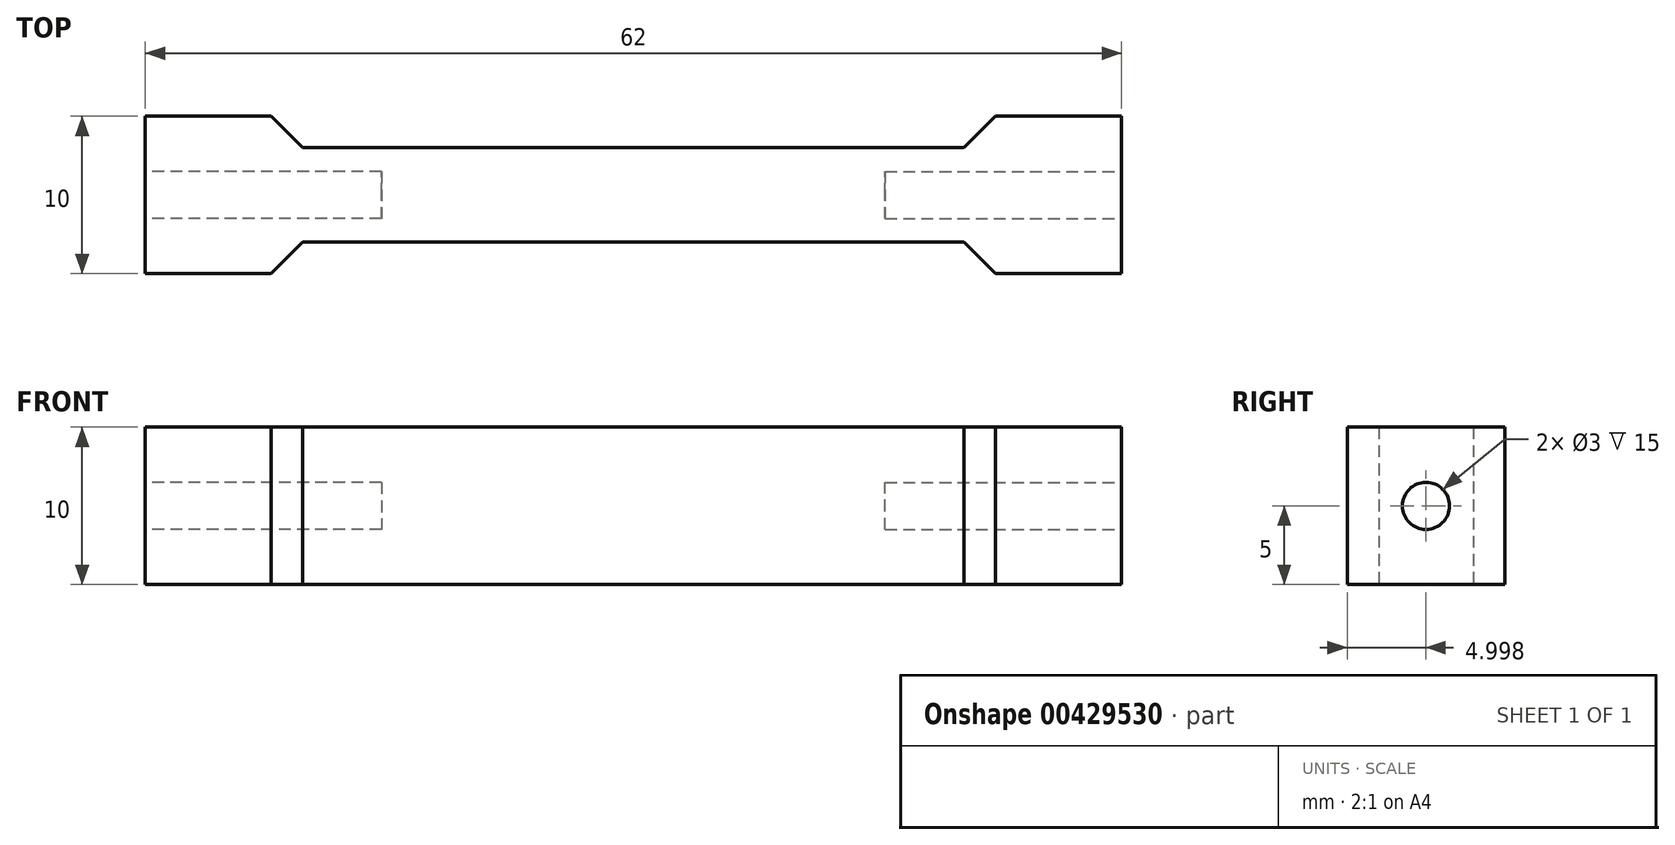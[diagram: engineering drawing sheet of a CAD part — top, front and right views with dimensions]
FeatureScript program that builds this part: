
annotation { "Feature Type Name" : "Feature", "Feature Type Description" : "" }
export const myFeature = defineFeature(function(context is Context, id is Id, definition is map)
    precondition{}
    {
        {
            var Q0;
            Q0=qCreatedBy(makeId("Top.planeOp"),FACE);
            var sketch = newSketch(context, id + "F0", { "sketchPlane" : qUnion([Q0])});
            skLineSegment(sketch, "E0", {"start": v(-25.31, 8.34) * mm, "end": v(-15.31, 8.34) * mm});
            skLineSegment(sketch, "E1", {"start": v(36.69, 8.34) * mm, "end": v(36.69, -1.66) * mm});
            skLineSegment(sketch, "E2", {"start": v(36.69, -1.66) * mm, "end": v(26.69, -1.66) * mm});
            skLineSegment(sketch, "E3", {"start": v(-25.31, -1.66) * mm, "end": v(-25.31, 8.34) * mm});
            skLineSegment(sketch, "E4.0", {"start": v(-15.31, 6.34) * mm, "end": v(26.69, 6.34) * mm});
            skLineSegment(sketch, "E5.0", {"start": v(26.69, 0.34) * mm, "end": v(-15.31, 0.34) * mm});
            skLineSegment(sketch, "E6", {"start": v(26.69, 8.34) * mm, "end": v(26.69, 6.34) * mm});
            skLineSegment(sketch, "E7", {"start": v(-15.31, 8.34) * mm, "end": v(-15.31, 6.34) * mm});
            skLineSegment(sketch, "E8.trimOffspring", {"start": v(26.69, 8.34) * mm, "end": v(36.69, 8.34) * mm});
            skLineSegment(sketch, "E9.trimOffspring", {"start": v(-15.31, -1.66) * mm, "end": v(-25.31, -1.66) * mm});
            skPoint(sketch, "E10.orphan", {"position": v(-15.31, -8.04) * mm});
            skPoint(sketch, "E11.orphan", {"position": v(26.69, -8.04) * mm});
            skLineSegment(sketch, "E12.trimOffspring", {"start": v(26.69, 0.34) * mm, "end": v(26.69, -1.66) * mm});
            skLineSegment(sketch, "E13.trimOffspring", {"start": v(-15.31, 0.34) * mm, "end": v(-15.31, -1.66) * mm});
            skPoint(sketch, "E14.orphan", {"position": v(-25.31, 0.34) * mm});
            skSolve(sketch);
        }
        {
            var Q0;
            Q0=makeQuery(id+"F0.imprint","IMPRINT",FACE,{"disambiguationData":[TD([[makeQuery(id+"F0.imprint","IMPRINT",EDGE,{"derivedFrom":sQuery(id+"F0.wireOp",EDGE,"E0")}),-1.0]])]});
            extrude(context, id + "F1", {"entities" : qUnion([Q0]), "depth" : 10 * mm});
        }
        {
            var Q0;
            Q0=makeQuery(id+"F1.opExtrude","SWEPT_EDGE",EDGE,{"disambiguationData":[OSD([sQuery(id+"F0.wireOp",EDGE,"E0"),sQuery(id+"F0.wireOp",EDGE,"E7")])]});
            var Q1;
            Q1=makeQuery(id+"F1.opExtrude","SWEPT_EDGE",EDGE,{"disambiguationData":[OSD([sQuery(id+"F0.wireOp",EDGE,"E6"),sQuery(id+"F0.wireOp",EDGE,"E8.trimOffspring")])]});
            var Q2;
            Q2=makeQuery(id+"F1.opExtrude","SWEPT_EDGE",EDGE,{"disambiguationData":[OSD([sQuery(id+"F0.wireOp",EDGE,"E9.trimOffspring"),sQuery(id+"F0.wireOp",EDGE,"E13.trimOffspring")])]});
            var Q3;
            Q3=makeQuery(id+"F1.opExtrude","SWEPT_EDGE",EDGE,{"disambiguationData":[OSD([sQuery(id+"F0.wireOp",EDGE,"E2"),sQuery(id+"F0.wireOp",EDGE,"E12.trimOffspring")])]});
            chamfer(context, id + "F2", {"entities" : qUnion([Q0, Q1, Q2, Q3]), "width" : 2 * mm, "tangentPropagation" : true});
        }
        {
            var Q0;
            Q0=makeQuery(id+"F1.opExtrude","SWEPT_FACE",FACE,{"disambiguationData":[OSD([sQuery(id+"F0.wireOp",EDGE,"E1")])]});
            var sketch = newSketch(context, id + "F3", { "sketchPlane" : qUnion([Q0])});
            skCircle(sketch, "E15", {"center": v(3.34, 5) * mm, "radius": 1.5 * mm});
            skSolve(sketch);
        }
        {
            var Q0;
            Q0=makeQuery(id+"F3.imprint","IMPRINT",FACE,{"disambiguationData":[TD([[makeQuery(id+"F3.imprint","IMPRINT",EDGE,{"derivedFrom":sQuery(id+"F3.wireOp",EDGE,"E15")}),1.0]])]});
            extrude(context, id + "F4", {"entities" : qUnion([Q0]), "operationType" : NewBodyOperationType.REMOVE, "oppositeDirection" : true, "depth" : 15 * mm});
        }
        {
            var Q0;
            Q0=makeQuery(id+"F1.opExtrude","SWEPT_FACE",FACE,{"disambiguationData":[OSD([sQuery(id+"F0.wireOp",EDGE,"E3")])]});
            var sketch = newSketch(context, id + "F5", { "sketchPlane" : qUnion([Q0])});
            skCircle(sketch, "E16", {"center": v(-3.34, 5) * mm, "radius": 1.5 * mm});
            skSolve(sketch);
        }
        {
            var Q0;
            Q0=makeQuery(id+"F5.imprint","IMPRINT",FACE,{"disambiguationData":[TD([[makeQuery(id+"F5.imprint","IMPRINT",EDGE,{"derivedFrom":sQuery(id+"F5.wireOp",EDGE,"E16")}),1.0]])]});
            extrude(context, id + "F6", {"entities" : qUnion([Q0]), "operationType" : NewBodyOperationType.REMOVE, "oppositeDirection" : true, "depth" : 15 * mm});
        }
    });
